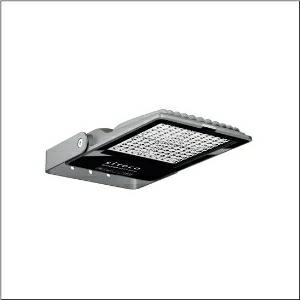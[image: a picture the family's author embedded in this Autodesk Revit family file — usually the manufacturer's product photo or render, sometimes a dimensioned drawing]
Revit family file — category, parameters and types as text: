
# Revit family: sicompact_r__31_mini___pl32_5xa7571c2k23_606d
name_source: partatom
category: Lighting Fixtures
units: mm (PartAtom-declared; Revit-internal decimal feet)

## family parameters
Cut with Voids When Loaded = No
Host = Face
Light Source = No
Part Type = Normal
Room Calculation Point = No
Round Connector Dimension = Use Diameter
Shared = No

## types (1)
- SiCompact® 31 mini  PL32 (1 x LED, 15000 lm, 95 W, 4000K)
    Apparent Load = 95 VA
    CIE Flux Codes = 32 69 98 100 100
    Color Rendering = 70
    Color Temperature = 4000K
    Default Elevation = 1800 mm
    Description = SiCompact® 31 mini, floodlight, primary light control with lens, of plastic, of toughened safety glass, transparent, light distribution: PL32, light emission: direct distribution, primary light characteristic: asymmetric, installation type: surface-mounted, LED, High Power LED, rated luminous flux: 15.000lm, luminous efficacy: 158lm/W, light colour: 740, colour temperature: 4000K, control gear: ECG, with cable, 3x 1.5mm², mains connection: 220..240V, AC, 50/60Hz, connection cable pre-assembled, cable length: 2m, rated input power: 95W, of diecast aluminium, specular, metallic grey (RAL 9006), length: 461mm, width: 261mm, height: 62mm, bracket, of sheet steel, coated, metallic grey (RAL 9006), ON/OFF, protection rating (complete): IP66, insulation class (complete): insulation class I (protective earthing), certification: CE, impact resistance: IK08, permissible operating ambient temperature: -40..+45°C, packaging unit: 1 piece

Light Distribution: PL32
    Height = 62 mm  [stored 0.203412 ft]
    Lamp = 1 x LED
    Lamp Light Flux = 15000 lm
    Lamp Power = 95 W
    Lamp count = 1
    Length = 460 mm
    Luminous efficacy = 158 lm/W
    Manufacturer = Siteco
    ModVariant = No
    Model = 5XA7571C2K23
    Number of Poles = 1
    OnlyDefault = Yes
    Power Factor = 1
    Product Name = SiCompact® 31 mini | PL32
    Product group = floodlight | pylon top
    ProductGroupID = 6101
    Protection Class = Protection class I
    Protection Degree = IP 66
    RLX_Detail_Level = 1
    RlxData = <blob elided: 126645 chars, md5=0c1be886>
    Socket = socket
    Standby Power = 0 W
    System Light Flux = 15000 lm
    System Power = 95 W
    Type Comments = Product without accessories
    Type Image = l_1006951.jpg
    URL = http://relux.com
    VarID = ---
    Voltage = 0 V
    Weight = 0.00 kg
    Width = 260 mm

note: [stored X ft] marks values corroborated as IEEE doubles in the binary element streams (Revit-internal decimal feet)

## geometry (parser evidence)
native form markers: Blend x4, Sweep x16
no freeform markers — native parametric forms only
